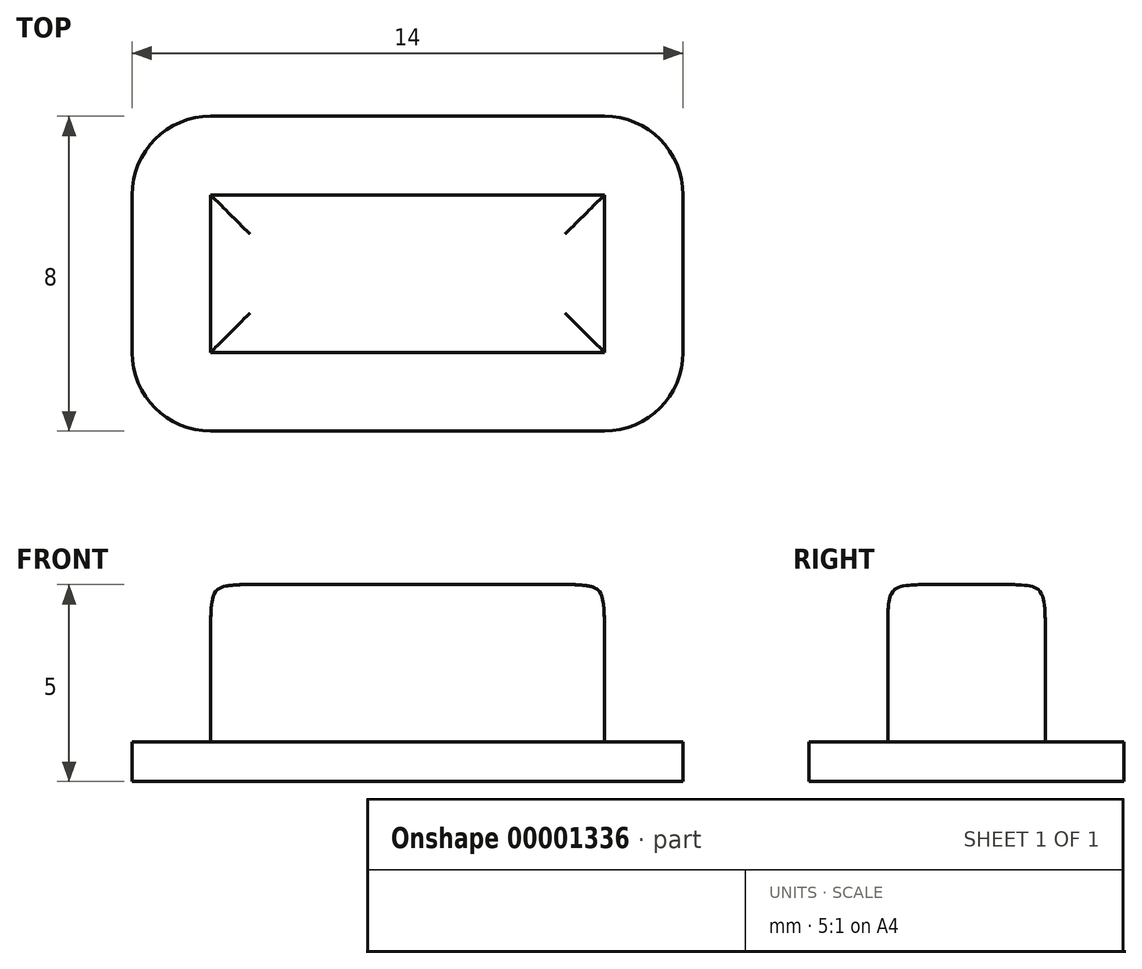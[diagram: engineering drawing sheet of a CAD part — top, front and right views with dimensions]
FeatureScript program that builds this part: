
annotation { "Feature Type Name" : "Feature", "Feature Type Description" : "" }
export const myFeature = defineFeature(function(context is Context, id is Id, definition is map)
    precondition{}
    {
        {
            var Q0;
            Q0=qCreatedBy(makeId("Top.planeOp"),FACE);
            var sketch = newSketch(context, id + "F0", { "sketchPlane" : qUnion([Q0])});
            skLineSegment(sketch, "E0.bottom", {"start": v(0, 0) * mm, "end": v(10, 0) * mm});
            skLineSegment(sketch, "E0.top", {"start": v(0, 4) * mm, "end": v(10, 4) * mm});
            skLineSegment(sketch, "E0.left", {"start": v(0, 0) * mm, "end": v(0, 4) * mm});
            skLineSegment(sketch, "E0.right", {"start": v(10, 0) * mm, "end": v(10, 4) * mm});
            skSolve(sketch);
        }
        {
            var Q0;
            Q0=makeQuery(id+"F0.imprint","IMPRINT",FACE,{"disambiguationData":[TD([[makeQuery(id+"F0.imprint","IMPRINT",EDGE,{"derivedFrom":sQuery(id+"F0.wireOp",EDGE,"E0.bottom")}),1.0]])]});
            extrude(context, id + "F1", {"entities" : qUnion([Q0]), "depth" : 4 * mm});
        }
        {
            var Q0;
            Q0=makeQuery(id+"F1.opExtrude","CAP_FACE",FACE,{"disambiguationData":[OSD([sQuery(id+"F0.wireOp",EDGE,"E0.bottom"),sQuery(id+"F0.wireOp",EDGE,"E0.top"),sQuery(id+"F0.wireOp",EDGE,"E0.left"),sQuery(id+"F0.wireOp",EDGE,"E0.right")])],"isStart":true});
            var sketch = newSketch(context, id + "F2", { "sketchPlane" : qUnion([Q0])});
            skLineSegment(sketch, "E1.0", {"start": v(0, 0) * mm, "end": v(10, 0) * mm});
            skLineSegment(sketch, "E1.1", {"start": v(0, 0) * mm, "end": v(0, -4) * mm});
            skLineSegment(sketch, "E1.2", {"start": v(0, -4) * mm, "end": v(10, -4) * mm});
            skLineSegment(sketch, "E1.3", {"start": v(10, 0) * mm, "end": v(10, -4) * mm});
            skLineSegment(sketch, "E2.0", {"start": v(-2, 2) * mm, "end": v(12, 2) * mm});
            skLineSegment(sketch, "E2.1", {"start": v(-2, 2) * mm, "end": v(-2, -6) * mm});
            skLineSegment(sketch, "E2.2", {"start": v(-2, -6) * mm, "end": v(12, -6) * mm});
            skLineSegment(sketch, "E2.3", {"start": v(12, 2) * mm, "end": v(12, -6) * mm});
            skSolve(sketch);
        }
        {
            var Q0;
            Q0=makeQuery(id+"F2.imprint","IMPRINT",FACE,{"disambiguationData":[TD([[makeQuery(id+"F2.imprint","IMPRINT",EDGE,{"derivedFrom":sQuery(id+"F2.wireOp",EDGE,"E1.0")}),1.0]])]});
            var Q1;
            Q1=makeQuery(id+"F2.imprint","IMPRINT",FACE,{"disambiguationData":[TD([[makeQuery(id+"F2.imprint","IMPRINT",EDGE,{"derivedFrom":sQuery(id+"F2.wireOp",EDGE,"E1.0")}),-1.0]])]});
            extrude(context, id + "F3", {"entities" : qUnion([Q0, Q1]), "operationType" : NewBodyOperationType.ADD, "depth" : 1 * mm});
        }
        {
            var Q0;
            Q0=makeQuery(id+"F1.opExtrude","CAP_FACE",FACE,{"disambiguationData":[OSD([sQuery(id+"F0.wireOp",EDGE,"E0.bottom"),sQuery(id+"F0.wireOp",EDGE,"E0.top"),sQuery(id+"F0.wireOp",EDGE,"E0.left"),sQuery(id+"F0.wireOp",EDGE,"E0.right")])],"isStart":false});
            fillet(context, id + "F4", {"entities" : qUnion([Q0]), "radius" : 1 * mm, "tangentPropagation" : true, "rho" : 0.7, "crossSection" : FilletCrossSection.CONIC, "allowEdgeOverflow" : false});
        }
        {
            var Q0;
            Q0=makeQuery(id+"F3.opExtrude","SWEPT_EDGE",EDGE,{"disambiguationData":[OSD([sQuery(id+"F2.wireOp",EDGE,"E2.0"),sQuery(id+"F2.wireOp",EDGE,"E2.3")])]});
            var Q1;
            Q1=makeQuery(id+"F3.opExtrude","SWEPT_EDGE",EDGE,{"disambiguationData":[OSD([sQuery(id+"F2.wireOp",EDGE,"E2.0"),sQuery(id+"F2.wireOp",EDGE,"E2.1")])]});
            var Q2;
            Q2=makeQuery(id+"F3.opExtrude","SWEPT_EDGE",EDGE,{"disambiguationData":[OSD([sQuery(id+"F2.wireOp",EDGE,"E2.1"),sQuery(id+"F2.wireOp",EDGE,"E2.2")])]});
            var Q3;
            Q3=makeQuery(id+"F3.opExtrude","SWEPT_EDGE",EDGE,{"disambiguationData":[OSD([sQuery(id+"F2.wireOp",EDGE,"E2.2"),sQuery(id+"F2.wireOp",EDGE,"E2.3")])]});
            fillet(context, id + "F5", {"entities" : qUnion([Q0, Q1, Q2, Q3]), "radius" : 2 * mm, "tangentPropagation" : true, "allowEdgeOverflow" : false});
        }
    });
